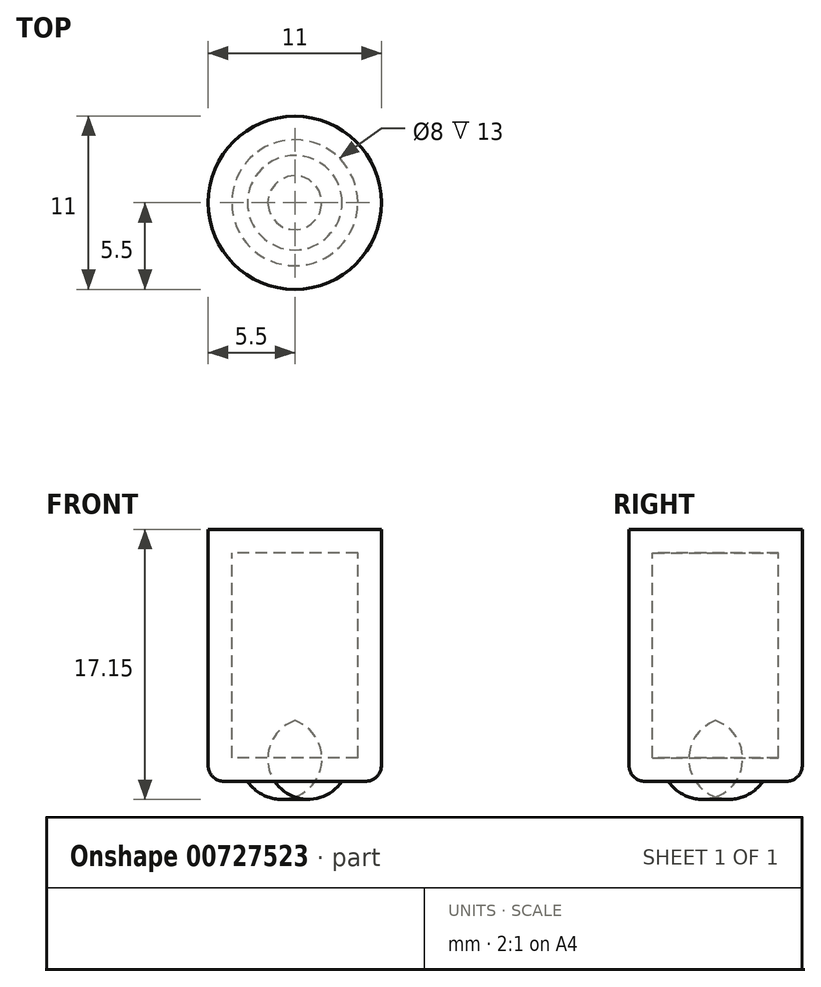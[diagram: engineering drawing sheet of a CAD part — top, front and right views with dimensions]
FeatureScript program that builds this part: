
annotation { "Feature Type Name" : "Feature", "Feature Type Description" : "" }
export const myFeature = defineFeature(function(context is Context, id is Id, definition is map)
    precondition{}
    {
        {
            var Q0;
            Q0=qCreatedBy(makeId("Top.planeOp"),FACE);
            var sketch = newSketch(context, id + "F0", { "sketchPlane" : qUnion([Q0])});
            skCircle(sketch, "E0", {"center": v(0, 0) * mm, "radius": 5.5 * mm});
            skSolve(sketch);
        }
        {
            var Q0;
            Q0 = qSketchRegion(id + "F0", true);
            extrude(context, id + "F1", {"entities" : qUnion([Q0]), "oppositeDirection" : true, "depth" : 16 * mm, "offsetDistance" : 25 * mm});
        }
        {
            var Q0;
            Q0=makeQuery(id+"F1.opExtrude","CAP_EDGE",EDGE,{"disambiguationData":[OSD([sQuery(id+"F0.wireOp",EDGE,"E0")])],"isStart":false});
            fillet(context, id + "F2", {"entities" : qUnion([Q0]), "radius" : 1 * mm, "tangentPropagation" : true, "allowEdgeOverflow" : false});
        }
        {
            var Q0;
            Q0=makeQuery(id+"F1.opExtrude","SWEPT_FACE",FACE,{"disambiguationData":[OSD([sQuery(id+"F0.wireOp",EDGE,"E0")])]});
            var Q1;
            Q1=makeQuery(id+"F1.opExtrude","SWEPT_BODY",BODY,{"disambiguationData":[OSD([sQuery(id+"F0.wireOp",EDGE,"E0")])]});
            shell(context, id + "F3", {"isHollow" : true, "entities" : qUnion([Q0]), "parts" : qUnion([Q1]), "thickness" : 1.5 * mm});
        }
        {
            var Q0;
            Q0=qCreatedBy(makeId("Front.planeOp"),FACE);
            var sketch = newSketch(context, id + "F4", { "sketchPlane" : qUnion([Q0])});
            skLineSegment(sketch, "E1", {"start": v(0, -16) * mm, "end": v(0, -17) * mm});
            skArc(sketch, "E2", {"start": v(0, -17) * mm, "mid": v(1.67, -17.01) * mm, "end": v(3, -16) * mm});
            skLineSegment(sketch, "E3", {"start": v(0, -16) * mm, "end": v(3, -16) * mm});
            skSolve(sketch);
        }
        {
            var Q0;
            Q0=makeQuery(id+"F4.imprint","IMPRINT",FACE,{"disambiguationData":[TD([[makeQuery(id+"F4.imprint","IMPRINT",EDGE,{"derivedFrom":sQuery(id+"F4.wireOp",EDGE,"E1")}),1.0]])]});
            var Q1;
            Q1=sQuery(id+"F4.wireOp",EDGE,"E1");
            revolve(context, id + "F5", {"operationType" : NewBodyOperationType.ADD, "surfaceOperationType" : NewSurfaceOperationType.NEW, "entities" : qUnion([Q0]), "axis" : qUnion([Q1]), "revolveType" : RevolveType.FULL});
        }
    });
